# Revit family: Plumbing-Lavatories-Sloan-Valve-SS3026_
name_source: partatom
category: Plumbing Fixtures
units: mm (PartAtom-declared; Revit-internal decimal feet)

## family parameters
Cut with Voids When Loaded = Yes
Host = Face
OmniClass Number = 23.45.05.14.14
OmniClass Title = Sinks/Lavatories
Part Type = Normal
Room Calculation Point = No
Round Connector Dimension = Use Diameter
Shared = No

## types (1)
- SS-3026
    Assembly Code = D2010400
    CW Connection = Yes
    CWFU = 1.5
    Cold Water Connection Diameter = 1"
    Cold Water Connector Description = Cold Water Connector d1/2"
    Default Elevation = 0"
    Depth = 18 1/2"
    Description = Vitreous China Vessel Lavatory.
    Edition number = 1
    HW Connection = Yes
    HWFU = 1.5
    Height = 6 3/4"
    Hot Water Connection Diameter = 1"
    Hot Water Connector Description = Hot Water Connector d1/2"
    Keynote = 10000
    Manufacturer = Sloan Valve
    Model = SS-3026
    Part Number = 3873026
    Product Material = Sloan Valve - Vitreous China - White
    Product data url = https://bimobject.com
    Sanitary Drain Connection Diameter = 2"
    Sanitary Drain Connector Description = Sanitary Drain Connector d1 1/2"
    URL = www.sloanvalve.com
    Valve Pressure Drop = 0.00 psi
    Vent Connection = Yes
    WFU = 2
    Waste Connection = Yes
    Water Flow = 0 GPM
    Width = 18 1/2"

## geometry (parser evidence)
native form markers: Sweep x1
no freeform markers — native parametric forms only
